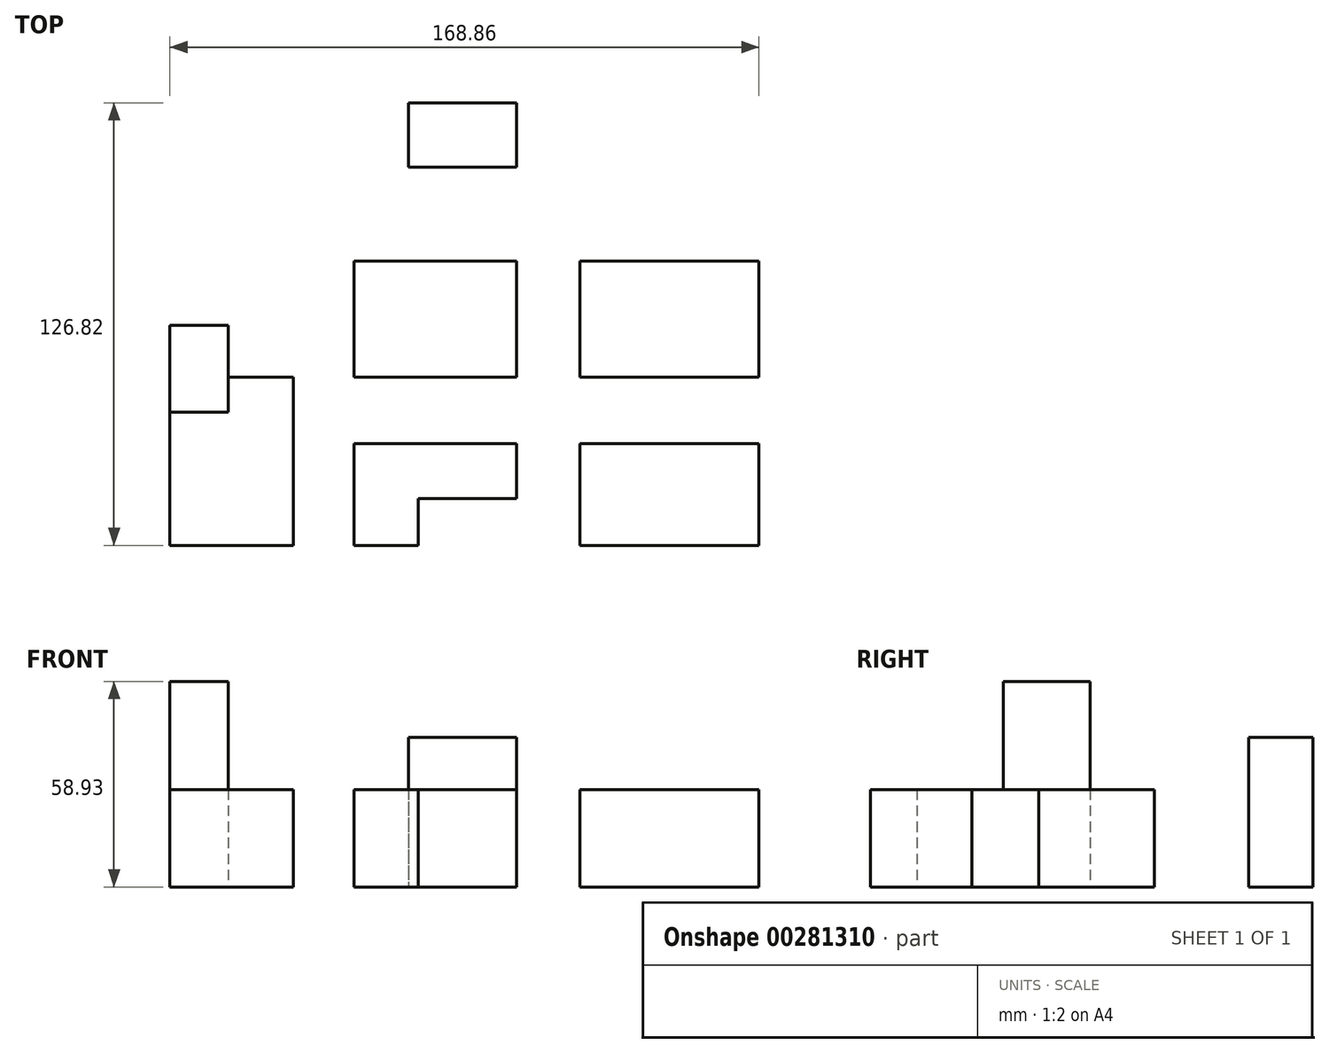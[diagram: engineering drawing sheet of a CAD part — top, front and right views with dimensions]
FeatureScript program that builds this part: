
annotation { "Feature Type Name" : "Feature", "Feature Type Description" : "" }
export const myFeature = defineFeature(function(context is Context, id is Id, definition is map)
    precondition{}
    {
        {
            var Q0;
            Q0=qCreatedBy(makeId("Top.planeOp"),FACE);
            var sketch = newSketch(context, id + "F0", { "sketchPlane" : qUnion([Q0])});
            skLineSegment(sketch, "E0.bottom", {"start": v(24.84, 33.2) * mm, "end": v(76.19, 33.2) * mm});
            skLineSegment(sketch, "E0.top", {"start": v(24.84, 0) * mm, "end": v(76.19, 0) * mm});
            skLineSegment(sketch, "E0.left", {"start": v(24.84, 33.2) * mm, "end": v(24.84, 0) * mm});
            skLineSegment(sketch, "E0.right", {"start": v(76.19, 33.2) * mm, "end": v(76.19, 0) * mm});
            skLineSegment(sketch, "E1.bottom", {"start": v(24.84, -19.1) * mm, "end": v(76.19, -19.1) * mm});
            skLineSegment(sketch, "E1.top", {"start": v(24.84, -48.24) * mm, "end": v(76.19, -48.24) * mm});
            skLineSegment(sketch, "E1.left", {"start": v(24.84, -19.1) * mm, "end": v(24.84, -48.24) * mm});
            skLineSegment(sketch, "E1.right", {"start": v(76.19, -19.1) * mm, "end": v(76.19, -48.24) * mm});
            skLineSegment(sketch, "E2.bottom", {"start": v(6.69, 0) * mm, "end": v(-39.89, 0) * mm});
            skLineSegment(sketch, "E2.top", {"start": v(6.69, 33.2) * mm, "end": v(-39.89, 33.2) * mm});
            skLineSegment(sketch, "E2.left", {"start": v(6.69, 0) * mm, "end": v(6.69, 33.2) * mm});
            skLineSegment(sketch, "E2.right", {"start": v(-39.89, 0) * mm, "end": v(-39.89, 33.2) * mm});
            skLineSegment(sketch, "E3", {"start": v(6.69, -19.1) * mm, "end": v(6.69, -34.87) * mm});
            skLineSegment(sketch, "E4", {"start": v(6.69, -34.87) * mm, "end": v(-21.5, -34.87) * mm});
            skLineSegment(sketch, "E5", {"start": v(-21.5, -34.87) * mm, "end": v(-21.5, -48.24) * mm});
            skLineSegment(sketch, "E6", {"start": v(-21.5, -48.24) * mm, "end": v(-39.89, -48.24) * mm});
            skLineSegment(sketch, "E7", {"start": v(-39.89, -48.24) * mm, "end": v(-39.89, -19.1) * mm});
            skLineSegment(sketch, "E8", {"start": v(-39.89, -19.1) * mm, "end": v(6.69, -19.1) * mm});
            skLineSegment(sketch, "E9.bottom", {"start": v(-57.32, 0) * mm, "end": v(-75.95, 0) * mm});
            skLineSegment(sketch, "E9.top", {"start": v(-57.32, -48.24) * mm, "end": v(-92.67, -48.24) * mm});
            skLineSegment(sketch, "E9.left", {"start": v(-57.32, 0) * mm, "end": v(-57.32, -48.24) * mm});
            skLineSegment(sketch, "E9.right", {"start": v(-92.67, -9.08) * mm, "end": v(-92.67, -48.24) * mm});
            skLineSegment(sketch, "E10.bottom", {"start": v(-92.67, 14.8) * mm, "end": v(-75.95, 14.8) * mm});
            skLineSegment(sketch, "E10.top", {"start": v(-92.67, -9.08) * mm, "end": v(-75.95, -9.08) * mm});
            skLineSegment(sketch, "E10.left", {"start": v(-92.67, 14.8) * mm, "end": v(-92.67, -9.08) * mm});
            skLineSegment(sketch, "E10.right", {"start": v(-75.95, 14.8) * mm, "end": v(-75.95, -9.08) * mm});
            skLineSegment(sketch, "E11.bottom", {"start": v(6.69, 60.19) * mm, "end": v(-24.24, 60.19) * mm});
            skLineSegment(sketch, "E11.top", {"start": v(6.69, 78.58) * mm, "end": v(-24.24, 78.58) * mm});
            skLineSegment(sketch, "E11.left", {"start": v(6.69, 60.19) * mm, "end": v(6.69, 78.58) * mm});
            skLineSegment(sketch, "E11.right", {"start": v(-24.24, 60.19) * mm, "end": v(-24.24, 78.58) * mm});
            skSolve(sketch);
        }
        {
            var Q0;
            Q0=makeQuery(id+"F0.imprint","IMPRINT",FACE,{"disambiguationData":[TD([[makeQuery(id+"F0.imprint","IMPRINT",EDGE,{"derivedFrom":sQuery(id+"F0.wireOp",EDGE,"E0.bottom")}),-1.0]])]});
            extrude(context, id + "F1", {"entities" : qUnion([Q0]), "depth" : 20.32 * mm});
        }
        {
            var Q0;
            Q0 = qSketchRegion(id + "F0", true);
            extrude(context, id + "F2", {"entities" : qUnion([Q0]), "operationType" : NewBodyOperationType.ADD, "depth" : 27.94 * mm});
        }
        {
            var Q0;
            Q0=makeQuery(id+"F2.opExtrude","CAP_FACE",FACE,{"disambiguationData":[OSD([sQuery(id+"F0.wireOp",EDGE,"E9.bottom"),sQuery(id+"F0.wireOp",EDGE,"E9.top"),sQuery(id+"F0.wireOp",EDGE,"E9.left"),sQuery(id+"F0.wireOp",EDGE,"E9.right"),sQuery(id+"F0.wireOp",EDGE,"E10.bottom"),sQuery(id+"F0.wireOp",EDGE,"E10.left"),sQuery(id+"F0.wireOp",EDGE,"E10.right")])],"isStart":false});
            var sketch = newSketch(context, id + "F3", { "sketchPlane" : qUnion([Q0])});
            skLineSegment(sketch, "E12.bottom", {"start": v(-92.67, 14.8) * mm, "end": v(-75.95, 14.8) * mm});
            skLineSegment(sketch, "E12.top", {"start": v(-92.67, -10.1) * mm, "end": v(-75.95, -10.1) * mm});
            skLineSegment(sketch, "E12.left", {"start": v(-92.67, 14.8) * mm, "end": v(-92.67, -10.1) * mm});
            skLineSegment(sketch, "E12.right", {"start": v(-75.95, 14.8) * mm, "end": v(-75.95, -10.1) * mm});
            skSolve(sketch);
        }
        {
            var Q0;
            {var subQ2=sQuery(id+"F3.wireOp",EDGE,"E12.bottom");Q0=makeQuery(id+"F3.imprint","IMPRINT",FACE,{"disambiguationData":[TD([[makeQuery(id+"F3.imprint","IMPRINT",EDGE,{"derivedFrom":subQ2}),-1.0]])]});}
            extrude(context, id + "F4", {"entities" : qUnion([Q0]), "operationType" : NewBodyOperationType.ADD, "depth" : 30.99 * mm});
        }
        {
            var Q0;
            Q0=makeQuery(id+"F2.opExtrude","CAP_FACE",FACE,{"disambiguationData":[OSD([sQuery(id+"F0.wireOp",EDGE,"E11.bottom"),sQuery(id+"F0.wireOp",EDGE,"E11.top"),sQuery(id+"F0.wireOp",EDGE,"E11.left"),sQuery(id+"F0.wireOp",EDGE,"E11.right")])],"isStart":false});
            extrude(context, id + "F5", {"entities" : qUnion([Q0]), "operationType" : NewBodyOperationType.ADD, "depth" : 15 * mm});
        }
    });
